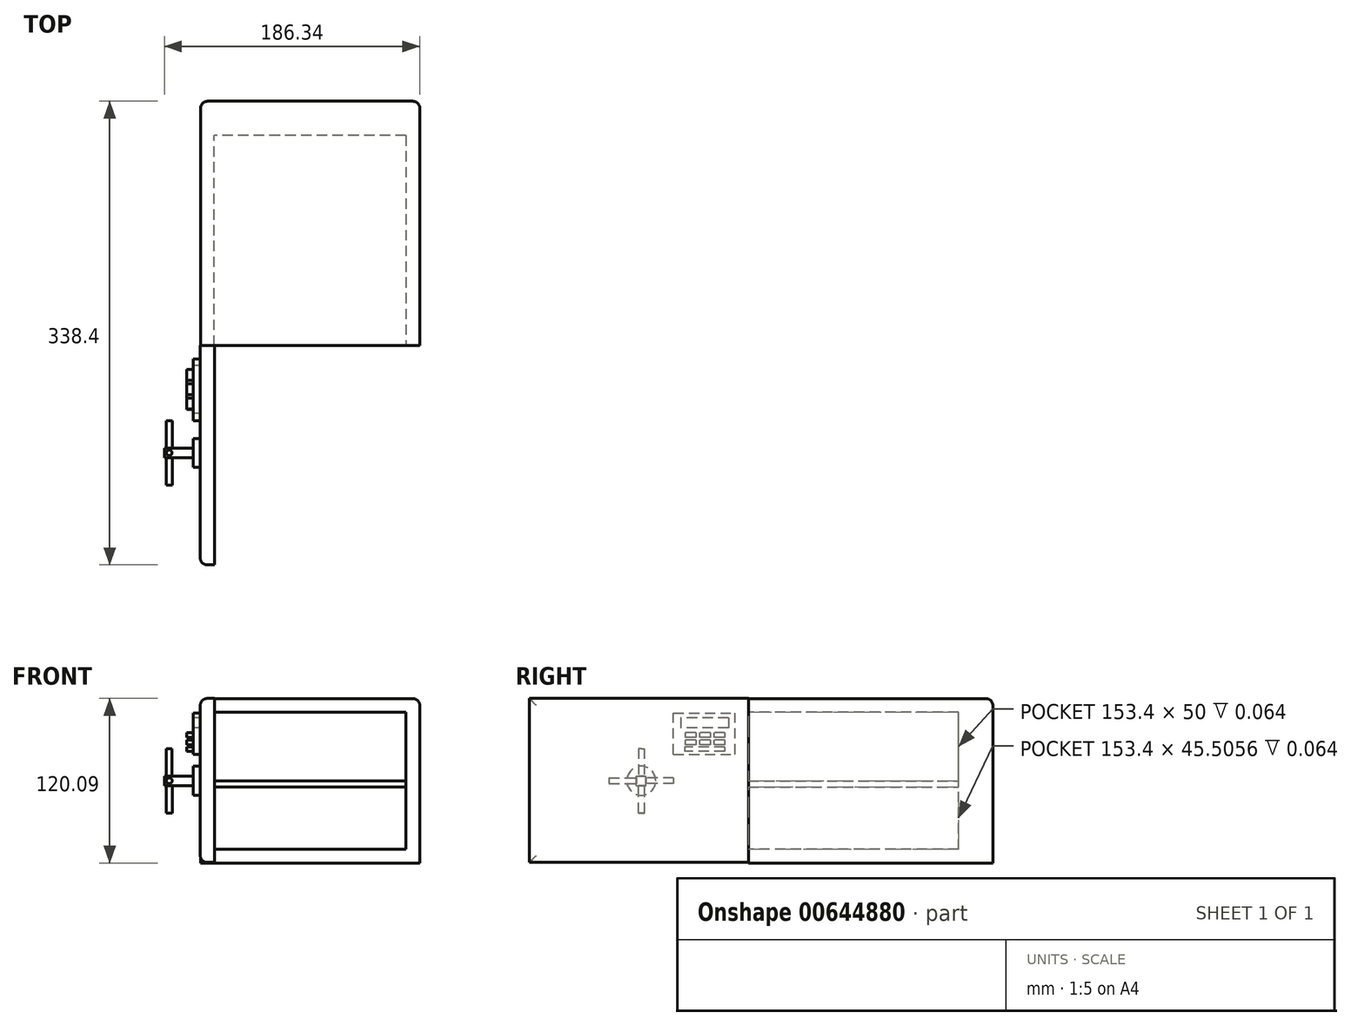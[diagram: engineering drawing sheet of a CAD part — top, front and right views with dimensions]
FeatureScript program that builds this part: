
annotation { "Feature Type Name" : "Feature", "Feature Type Description" : "" }
export const myFeature = defineFeature(function(context is Context, id is Id, definition is map)
    precondition{}
    {
        {
            var Q0;
            Q0=qCreatedBy(makeId("Front.planeOp"),FACE);
            var sketch = newSketch(context, id + "F0", { "sketchPlane" : qUnion([Q0])});
            skLineSegment(sketch, "E0.bottom", {"start": v(80, -60) * mm, "end": v(-80, -60) * mm});
            skLineSegment(sketch, "E0.top", {"start": v(80, 60) * mm, "end": v(-80, 60) * mm});
            skLineSegment(sketch, "E0.left", {"start": v(80, -60) * mm, "end": v(80, 60) * mm});
            skLineSegment(sketch, "E0.right", {"start": v(-80, -60) * mm, "end": v(-80, 60) * mm});
            skPoint(sketch, "E0.middle", {"position": v(0, 0) * mm});
            skLineSegment(sketch, "E1.bottom", {"start": v(70, -50) * mm, "end": v(-70, -50) * mm});
            skLineSegment(sketch, "E1.top", {"start": v(70, 50) * mm, "end": v(-70, 50) * mm});
            skLineSegment(sketch, "E1.left", {"start": v(70, -50) * mm, "end": v(70, 50) * mm});
            skLineSegment(sketch, "E1.right", {"start": v(-70, -50) * mm, "end": v(-70, 50) * mm});
            skSolve(sketch);
        }
        {
            var Q0;
            Q0 = qSketchRegion(id + "F0", true);
            extrude(context, id + "F1", {"entities" : qUnion([Q0]), "oppositeDirection" : true, "depth" : 153.4 * mm, "offsetDistance" : 25 * mm});
        }
        {
            var Q0;
            Q0=makeQuery(id+"F1.opExtrude","CAP_FACE",FACE,{"disambiguationData":[OSD([sQuery(id+"F0.wireOp",EDGE,"E0.bottom"),sQuery(id+"F0.wireOp",EDGE,"E0.top"),sQuery(id+"F0.wireOp",EDGE,"E0.left"),sQuery(id+"F0.wireOp",EDGE,"E0.right"),sQuery(id+"F0.wireOp",EDGE,"E1.bottom"),sQuery(id+"F0.wireOp",EDGE,"E1.top"),sQuery(id+"F0.wireOp",EDGE,"E1.left"),sQuery(id+"F0.wireOp",EDGE,"E1.right")])],"isStart":false});
            var sketch = newSketch(context, id + "F2", { "sketchPlane" : qUnion([Q0])});
            skLineSegment(sketch, "E2.bottom", {"start": v(-80, 60) * mm, "end": v(80, 60) * mm});
            skLineSegment(sketch, "E2.top", {"start": v(-80, -60) * mm, "end": v(80, -60) * mm});
            skLineSegment(sketch, "E2.left", {"start": v(-80, 60) * mm, "end": v(-80, -60) * mm});
            skLineSegment(sketch, "E2.right", {"start": v(80, 60) * mm, "end": v(80, -60) * mm});
            skSolve(sketch);
        }
        {
            var Q0;
            Q0 = qSketchRegion(id + "F2", true);
            extrude(context, id + "F3", {"entities" : qUnion([Q0]), "operationType" : NewBodyOperationType.ADD, "depth" : 25 * mm, "offsetDistance" : 25 * mm});
        }
        {
            var Q0;
            Q0=makeQuery(id+"F1.opExtrude","CAP_FACE",FACE,{"disambiguationData":[OSD([sQuery(id+"F0.wireOp",EDGE,"E0.bottom"),sQuery(id+"F0.wireOp",EDGE,"E0.top"),sQuery(id+"F0.wireOp",EDGE,"E0.left"),sQuery(id+"F0.wireOp",EDGE,"E0.right"),sQuery(id+"F0.wireOp",EDGE,"E1.bottom"),sQuery(id+"F0.wireOp",EDGE,"E1.top"),sQuery(id+"F0.wireOp",EDGE,"E1.left"),sQuery(id+"F0.wireOp",EDGE,"E1.right")])],"isStart":true});
            var sketch = newSketch(context, id + "F4", { "sketchPlane" : qUnion([Q0])});
            skLineSegment(sketch, "E3.bottom", {"start": v(-80, 60) * mm, "end": v(80, 60) * mm});
            skLineSegment(sketch, "E3.top", {"start": v(-80, -60) * mm, "end": v(80, -60) * mm});
            skLineSegment(sketch, "E3.left", {"start": v(-80, 60) * mm, "end": v(-80, -60) * mm});
            skLineSegment(sketch, "E3.right", {"start": v(80, 60) * mm, "end": v(80, -60) * mm});
            skSolve(sketch);
        }
        {
            var Q0;
            Q0=makeQuery(id+"F4.imprint","IMPRINT",FACE,{"disambiguationData":[TD([[makeQuery(id+"F4.imprint","IMPRINT",EDGE,{"derivedFrom":sQuery(id+"F4.wireOp",EDGE,"E3.bottom")}),1.0]])]});
            var sketch = newSketch(context, id + "F5", { "sketchPlane" : qUnion([Q0])});
            skLineSegment(sketch, "E4.bottom", {"start": v(-77, 35) * mm, "end": v(-74, 35) * mm});
            skLineSegment(sketch, "E4.top", {"start": v(-77, 10) * mm, "end": v(-74, 10) * mm});
            skLineSegment(sketch, "E4.left", {"start": v(-77, 35) * mm, "end": v(-77, 10) * mm});
            skLineSegment(sketch, "E4.right", {"start": v(-74, 35) * mm, "end": v(-74, 10) * mm});
            skLineSegment(sketch, "E5.bottom", {"start": v(-77, -13.23) * mm, "end": v(-74.5, -13.23) * mm});
            skLineSegment(sketch, "E5.top", {"start": v(-77, -35) * mm, "end": v(-74.5, -35) * mm});
            skLineSegment(sketch, "E5.left", {"start": v(-77, -13.23) * mm, "end": v(-77, -35) * mm});
            skLineSegment(sketch, "E5.right", {"start": v(-74.5, -13.23) * mm, "end": v(-74.5, -35) * mm});
            skSolve(sketch);
        }
        {
            var Q0;
            Q0 = qSketchRegion(id + "F5", true);
            var Q1;
            Q1=sQuery(id+"F5.wireOp",EDGE,"E4.right");
            revolve(context, id + "F6", {"operationType" : NewBodyOperationType.ADD, "entities" : qUnion([Q0]), "axis" : qUnion([Q1]), "revolveType" : RevolveType.FULL});
        }
        {
            var Q0;
            Q0=makeQuery(id+"F4.imprint","IMPRINT",FACE,{"disambiguationData":[TD([[makeQuery(id+"F4.imprint","IMPRINT",EDGE,{"derivedFrom":sQuery(id+"F4.wireOp",EDGE,"E3.bottom")}),1.0]])]});
            var sketch = newSketch(context, id + "F7", { "sketchPlane" : qUnion([Q0])});
            skLineSegment(sketch, "E6.bottom", {"start": v(-80.24, 60.1) * mm, "end": v(-69.94, 60.1) * mm});
            skLineSegment(sketch, "E6.top", {"start": v(-80.24, -59.63) * mm, "end": v(-69.94, -59.63) * mm});
            skLineSegment(sketch, "E6.left", {"start": v(-80.24, 60.1) * mm, "end": v(-80.24, -59.63) * mm});
            skLineSegment(sketch, "E6.right", {"start": v(-69.94, 60.1) * mm, "end": v(-69.94, -59.63) * mm});
            skSolve(sketch);
        }
        {
            var Q0;
            Q0 = qSketchRegion(id + "F7", true);
            extrude(context, id + "F8", {"entities" : qUnion([Q0]), "operationType" : NewBodyOperationType.ADD, "depth" : 160 * mm, "offsetDistance" : 25 * mm});
        }
        {
            var Q0;
            Q0=makeQuery(id+"F8.opExtrude","SWEPT_FACE",FACE,{"disambiguationData":[OSD([sQuery(id+"F7.wireOp",EDGE,"E6.left")])]});
            var sketch = newSketch(context, id + "F9", { "sketchPlane" : qUnion([Q0])});
            skCircle(sketch, "E7", {"center": v(78.27, 0) * mm, "radius": 10.57 * mm});
            skSolve(sketch);
        }
        {
            var Q0;
            Q0 = qSketchRegion(id + "F9", true);
            extrude(context, id + "F10", {"entities" : qUnion([Q0]), "operationType" : NewBodyOperationType.ADD, "depth" : 5 * mm, "offsetDistance" : 25 * mm});
        }
        {
            var Q0;
            Q0=makeQuery(id+"F10.opExtrude","CAP_FACE",FACE,{"disambiguationData":[OSD([sQuery(id+"F9.wireOp",EDGE,"E7")])],"isStart":false});
            var sketch = newSketch(context, id + "F11", { "sketchPlane" : qUnion([Q0])});
            skLineSegment(sketch, "E8.bottom", {"start": v(81.77, -3.5) * mm, "end": v(74.77, -3.5) * mm});
            skLineSegment(sketch, "E8.top", {"start": v(81.77, 3.5) * mm, "end": v(74.77, 3.5) * mm});
            skLineSegment(sketch, "E8.left", {"start": v(81.77, -3.5) * mm, "end": v(81.77, 3.5) * mm});
            skLineSegment(sketch, "E8.right", {"start": v(74.77, -3.5) * mm, "end": v(74.77, 3.5) * mm});
            skPoint(sketch, "E8.middle", {"position": v(78.27, 0) * mm});
            skSolve(sketch);
        }
        {
            var Q0;
            Q0 = qSketchRegion(id + "F11", true);
            extrude(context, id + "F12", {"entities" : qUnion([Q0]), "operationType" : NewBodyOperationType.ADD, "depth" : 21.1 * mm, "offsetDistance" : 25 * mm});
        }
        {
            var Q0;
            Q0=makeQuery(id+"F12.opExtrude","SWEPT_FACE",FACE,{"disambiguationData":[OSD([sQuery(id+"F11.wireOp",EDGE,"E8.top")])]});
            var sketch = newSketch(context, id + "F13", { "sketchPlane" : qUnion([Q0])});
            skCircle(sketch, "E9", {"center": v(-102.93, -78.18) * mm, "radius": 2 * mm});
            skSolve(sketch);
        }
        {
            var Q0;
            Q0 = qSketchRegion(id + "F13", true);
            extrude(context, id + "F14", {"entities" : qUnion([Q0]), "operationType" : NewBodyOperationType.ADD, "depth" : 20 * mm, "offsetDistance" : 25 * mm});
        }
        {
            var Q0;
            Q0=makeQuery(id+"F12.opExtrude","SWEPT_FACE",FACE,{"disambiguationData":[OSD([sQuery(id+"F11.wireOp",EDGE,"E8.right")])]});
            var sketch = newSketch(context, id + "F15", { "sketchPlane" : qUnion([Q0])});
            skCircle(sketch, "E10", {"center": v(102.84, 0) * mm, "radius": 2.1 * mm});
            skSolve(sketch);
        }
        {
            var Q0;
            Q0 = qSketchRegion(id + "F15", true);
            extrude(context, id + "F16", {"entities" : qUnion([Q0]), "operationType" : NewBodyOperationType.ADD, "depth" : 20 * mm, "offsetDistance" : 25 * mm});
        }
        {
            var Q0;
            Q0=makeQuery(id+"F12.opExtrude","SWEPT_FACE",FACE,{"disambiguationData":[OSD([sQuery(id+"F11.wireOp",EDGE,"E8.left")])]});
            var sketch = newSketch(context, id + "F17", { "sketchPlane" : qUnion([Q0])});
            skCircle(sketch, "E11", {"center": v(-102.84, 0) * mm, "radius": 2.1 * mm});
            skSolve(sketch);
        }
        {
            var Q0;
            Q0 = qSketchRegion(id + "F17", true);
            extrude(context, id + "F18", {"entities" : qUnion([Q0]), "operationType" : NewBodyOperationType.ADD, "depth" : 20 * mm, "offsetDistance" : 25 * mm});
        }
        {
            var Q0;
            Q0=makeQuery(id+"F12.opExtrude","SWEPT_FACE",FACE,{"disambiguationData":[OSD([sQuery(id+"F11.wireOp",EDGE,"E8.bottom")])]});
            var sketch = newSketch(context, id + "F19", { "sketchPlane" : qUnion([Q0])});
            skCircle(sketch, "E12", {"center": v(-102.72, 78.16) * mm, "radius": 2.22 * mm});
            skSolve(sketch);
        }
        {
            var Q0;
            Q0 = qSketchRegion(id + "F19", true);
            extrude(context, id + "F20", {"entities" : qUnion([Q0]), "operationType" : NewBodyOperationType.ADD, "depth" : 20 * mm, "offsetDistance" : 25 * mm});
        }
        {
            var Q0;
            Q0=makeQuery(id+"F8.opExtrude","SWEPT_FACE",FACE,{"disambiguationData":[OSD([sQuery(id+"F7.wireOp",EDGE,"E6.left")])]});
            var sketch = newSketch(context, id + "F21", { "sketchPlane" : qUnion([Q0])});
            skLineSegment(sketch, "E13.bottom", {"start": v(54.8, 19.38) * mm, "end": v(9.8, 19.38) * mm});
            skLineSegment(sketch, "E13.top", {"start": v(54.8, 49.38) * mm, "end": v(9.8, 49.38) * mm});
            skLineSegment(sketch, "E13.left", {"start": v(54.8, 19.38) * mm, "end": v(54.8, 49.38) * mm});
            skLineSegment(sketch, "E13.right", {"start": v(9.8, 19.38) * mm, "end": v(9.8, 49.38) * mm});
            skPoint(sketch, "E13.middle", {"position": v(32.3, 34.38) * mm});
            skSolve(sketch);
        }
        {
            var Q0;
            Q0 = qSketchRegion(id + "F21", true);
            extrude(context, id + "F22", {"entities" : qUnion([Q0]), "operationType" : NewBodyOperationType.ADD, "depth" : 5 * mm, "offsetDistance" : 25 * mm});
        }
        {
            var Q0;
            Q0=makeQuery(id+"F22.opExtrude","CAP_FACE",FACE,{"disambiguationData":[OSD([sQuery(id+"F21.wireOp",EDGE,"E13.bottom"),sQuery(id+"F21.wireOp",EDGE,"E13.top"),sQuery(id+"F21.wireOp",EDGE,"E13.left"),sQuery(id+"F21.wireOp",EDGE,"E13.right")])],"isStart":false});
            var sketch = newSketch(context, id + "F23", { "sketchPlane" : qUnion([Q0])});
            skLineSegment(sketch, "E14.bottom", {"start": v(14.55, 45.88) * mm, "end": v(49.55, 45.88) * mm});
            skLineSegment(sketch, "E14.top", {"start": v(14.55, 38.67) * mm, "end": v(49.55, 38.67) * mm});
            skLineSegment(sketch, "E14.left", {"start": v(14.55, 45.88) * mm, "end": v(14.55, 38.67) * mm});
            skLineSegment(sketch, "E14.right", {"start": v(49.55, 45.88) * mm, "end": v(49.55, 38.67) * mm});
            skSolve(sketch);
        }
        {
            var Q0;
            Q0 = qSketchRegion(id + "F23", true);
            extrude(context, id + "F24", {"entities" : qUnion([Q0]), "operationType" : NewBodyOperationType.REMOVE, "oppositeDirection" : true, "depth" : 5 * mm, "offsetDistance" : 25 * mm});
        }
        {
            var Q0;
            Q0=makeQuery(id+"F22.opExtrude","CAP_FACE",FACE,{"disambiguationData":[OSD([sQuery(id+"F21.wireOp",EDGE,"E13.bottom"),sQuery(id+"F21.wireOp",EDGE,"E13.top"),sQuery(id+"F21.wireOp",EDGE,"E13.left"),sQuery(id+"F21.wireOp",EDGE,"E13.right")])],"isStart":false});
            var sketch = newSketch(context, id + "F25", { "sketchPlane" : qUnion([Q0])});
            skLineSegment(sketch, "E15.bottom", {"start": v(17.3, 35.17) * mm, "end": v(25.3, 35.17) * mm});
            skLineSegment(sketch, "E15.top", {"start": v(17.3, 31.67) * mm, "end": v(25.3, 31.67) * mm});
            skLineSegment(sketch, "E15.left", {"start": v(17.3, 35.17) * mm, "end": v(17.3, 31.67) * mm});
            skLineSegment(sketch, "E15.right", {"start": v(25.3, 35.17) * mm, "end": v(25.3, 31.67) * mm});
            skLineSegment(sketch, "E16.bottom", {"start": v(27.8, 35.17) * mm, "end": v(35.8, 35.17) * mm});
            skLineSegment(sketch, "E16.top", {"start": v(27.8, 31.67) * mm, "end": v(35.8, 31.67) * mm});
            skLineSegment(sketch, "E16.left", {"start": v(27.8, 35.17) * mm, "end": v(27.8, 31.67) * mm});
            skLineSegment(sketch, "E16.right", {"start": v(35.8, 35.17) * mm, "end": v(35.8, 31.67) * mm});
            skLineSegment(sketch, "E17.bottom", {"start": v(38.3, 35.17) * mm, "end": v(46.3, 35.17) * mm});
            skLineSegment(sketch, "E17.top", {"start": v(38.3, 31.67) * mm, "end": v(46.3, 31.67) * mm});
            skLineSegment(sketch, "E17.left", {"start": v(38.3, 35.17) * mm, "end": v(38.3, 31.67) * mm});
            skLineSegment(sketch, "E17.right", {"start": v(46.3, 35.17) * mm, "end": v(46.3, 31.67) * mm});
            skLineSegment(sketch, "E18.bottom", {"start": v(17.3, 29.67) * mm, "end": v(25.3, 29.67) * mm});
            skLineSegment(sketch, "E18.top", {"start": v(17.3, 26.17) * mm, "end": v(25.3, 26.17) * mm});
            skLineSegment(sketch, "E18.left", {"start": v(17.3, 29.67) * mm, "end": v(17.3, 26.17) * mm});
            skLineSegment(sketch, "E18.right", {"start": v(25.3, 29.67) * mm, "end": v(25.3, 26.17) * mm});
            skLineSegment(sketch, "E19.bottom", {"start": v(27.8, 29.67) * mm, "end": v(35.8, 29.67) * mm});
            skLineSegment(sketch, "E19.top", {"start": v(27.8, 26.17) * mm, "end": v(35.8, 26.17) * mm});
            skLineSegment(sketch, "E19.left", {"start": v(27.8, 29.67) * mm, "end": v(27.8, 26.17) * mm});
            skLineSegment(sketch, "E19.right", {"start": v(35.8, 29.67) * mm, "end": v(35.8, 26.17) * mm});
            skLineSegment(sketch, "E20.bottom", {"start": v(38.3, 29.67) * mm, "end": v(46.3, 29.67) * mm});
            skLineSegment(sketch, "E20.top", {"start": v(38.3, 26.17) * mm, "end": v(46.3, 26.17) * mm});
            skLineSegment(sketch, "E20.left", {"start": v(38.3, 29.67) * mm, "end": v(38.3, 26.17) * mm});
            skLineSegment(sketch, "E20.right", {"start": v(46.3, 29.67) * mm, "end": v(46.3, 26.17) * mm});
            skSolve(sketch);
        }
        {
            var Q0;
            Q0 = qSketchRegion(id + "F25", true);
            extrude(context, id + "F26", {"entities" : qUnion([Q0]), "operationType" : NewBodyOperationType.ADD, "depth" : 5 * mm, "offsetDistance" : 25 * mm});
        }
        {
            var Q0;
            Q0=makeQuery(id+"F4.imprint","IMPRINT",FACE,{"disambiguationData":[TD([[makeQuery(id+"F4.imprint","IMPRINT",EDGE,{"derivedFrom":makeQuery(id+"F1.opExtrude","CAP_EDGE",EDGE,{"disambiguationData":[OSD([sQuery(id+"F0.wireOp",EDGE,"E1.bottom")])],"isStart":true})}),-1.0]])]});
            var sketch = newSketch(context, id + "F27", { "sketchPlane" : qUnion([Q0])});
            skLineSegment(sketch, "E21.bottom", {"start": v(-70.24, 0) * mm, "end": v(69.76, 0) * mm});
            skLineSegment(sketch, "E21.top", {"start": v(-70.24, -4.5) * mm, "end": v(69.76, -4.5) * mm});
            skLineSegment(sketch, "E21.left", {"start": v(-70.24, 0) * mm, "end": v(-70.24, -4.5) * mm});
            skLineSegment(sketch, "E21.right", {"start": v(69.76, 0) * mm, "end": v(69.76, -4.5) * mm});
            skSolve(sketch);
        }
        {
            var Q0;
            Q0 = qSketchRegion(id + "F27", true);
            extrude(context, id + "F28", {"entities" : qUnion([Q0]), "operationType" : NewBodyOperationType.ADD, "oppositeDirection" : true, "depth" : 176 * mm, "offsetDistance" : 25 * mm});
        }
        {
            var Q0;
            Q0=makeQuery(id+"F22.opExtrude","CAP_FACE",FACE,{"disambiguationData":[OSD([sQuery(id+"F21.wireOp",EDGE,"E13.bottom"),sQuery(id+"F21.wireOp",EDGE,"E13.top"),sQuery(id+"F21.wireOp",EDGE,"E13.left"),sQuery(id+"F21.wireOp",EDGE,"E13.right")])],"isStart":false});
            var sketch = newSketch(context, id + "F29", { "sketchPlane" : qUnion([Q0])});
            skLineSegment(sketch, "E22.bottom", {"start": v(17.45, 24.76) * mm, "end": v(46.45, 24.76) * mm});
            skLineSegment(sketch, "E22.top", {"start": v(17.45, 21.56) * mm, "end": v(46.45, 21.56) * mm});
            skLineSegment(sketch, "E22.left", {"start": v(17.45, 24.76) * mm, "end": v(17.45, 21.56) * mm});
            skLineSegment(sketch, "E22.right", {"start": v(46.45, 24.76) * mm, "end": v(46.45, 21.56) * mm});
            skSolve(sketch);
        }
        {
            var Q0;
            Q0 = qSketchRegion(id + "F29", true);
            extrude(context, id + "F30", {"entities" : qUnion([Q0]), "operationType" : NewBodyOperationType.ADD, "depth" : 5 * mm, "offsetDistance" : 25 * mm});
        }
        {
            var Q0;
            Q0=makeQuery(id+"F3.boolean.opBoolean","MERGE",EDGE,{"derivedFrom":[makeQuery(id+"F1.opExtrude","SWEPT_EDGE",EDGE,{"disambiguationData":[OSD([sQuery(id+"F0.wireOp",EDGE,"E0.top"),sQuery(id+"F0.wireOp",EDGE,"E0.right")])]}),makeQuery(id+"F3.opExtrude","SWEPT_EDGE",EDGE,{"disambiguationData":[OSD([sQuery(id+"F2.wireOp",EDGE,"E2.bottom"),sQuery(id+"F2.wireOp",EDGE,"E2.right")])]})]});
            var Q1;
            Q1=makeQuery(id+"F3.opExtrude","CAP_EDGE",EDGE,{"disambiguationData":[OSD([sQuery(id+"F2.wireOp",EDGE,"E2.bottom")])],"isStart":false});
            var Q2;
            Q2=makeQuery(id+"F3.boolean.opBoolean","MERGE",EDGE,{"derivedFrom":[makeQuery(id+"F1.opExtrude","SWEPT_EDGE",EDGE,{"disambiguationData":[OSD([sQuery(id+"F0.wireOp",EDGE,"E0.top"),sQuery(id+"F0.wireOp",EDGE,"E0.left")])]}),makeQuery(id+"F3.opExtrude","SWEPT_EDGE",EDGE,{"disambiguationData":[OSD([sQuery(id+"F2.wireOp",EDGE,"E2.bottom"),sQuery(id+"F2.wireOp",EDGE,"E2.left")])]})]});
            var Q3;
            Q3=makeQuery(id+"F3.opExtrude","CAP_EDGE",EDGE,{"disambiguationData":[OSD([sQuery(id+"F2.wireOp",EDGE,"E2.left")])],"isStart":false});
            var Q4;
            Q4=makeQuery(id+"F3.opExtrude","CAP_EDGE",EDGE,{"disambiguationData":[OSD([sQuery(id+"F2.wireOp",EDGE,"E2.right")])],"isStart":false});
            fillet(context, id + "F31", {"entities" : qUnion([Q0, Q1, Q2, Q3, Q4]), "radius" : 5 * mm, "tangentPropagation" : true, "allowEdgeOverflow" : false});
        }
        {
            var Q0;
            Q0=makeQuery(id+"F8.opExtrude","SWEPT_EDGE",EDGE,{"disambiguationData":[OSD([sQuery(id+"F7.wireOp",EDGE,"E6.bottom"),sQuery(id+"F7.wireOp",EDGE,"E6.left")])]});
            var Q1;
            Q1=makeQuery(id+"F8.opExtrude","CAP_EDGE",EDGE,{"disambiguationData":[OSD([sQuery(id+"F7.wireOp",EDGE,"E6.left")])],"isStart":false});
            var Q2;
            Q2=makeQuery(id+"F8.opExtrude","SWEPT_EDGE",EDGE,{"disambiguationData":[OSD([sQuery(id+"F7.wireOp",EDGE,"E6.top"),sQuery(id+"F7.wireOp",EDGE,"E6.left")])]});
            fillet(context, id + "F32", {"entities" : qUnion([Q0, Q1, Q2]), "radius" : 5 * mm, "tangentPropagation" : true, "allowEdgeOverflow" : false});
        }
    });
